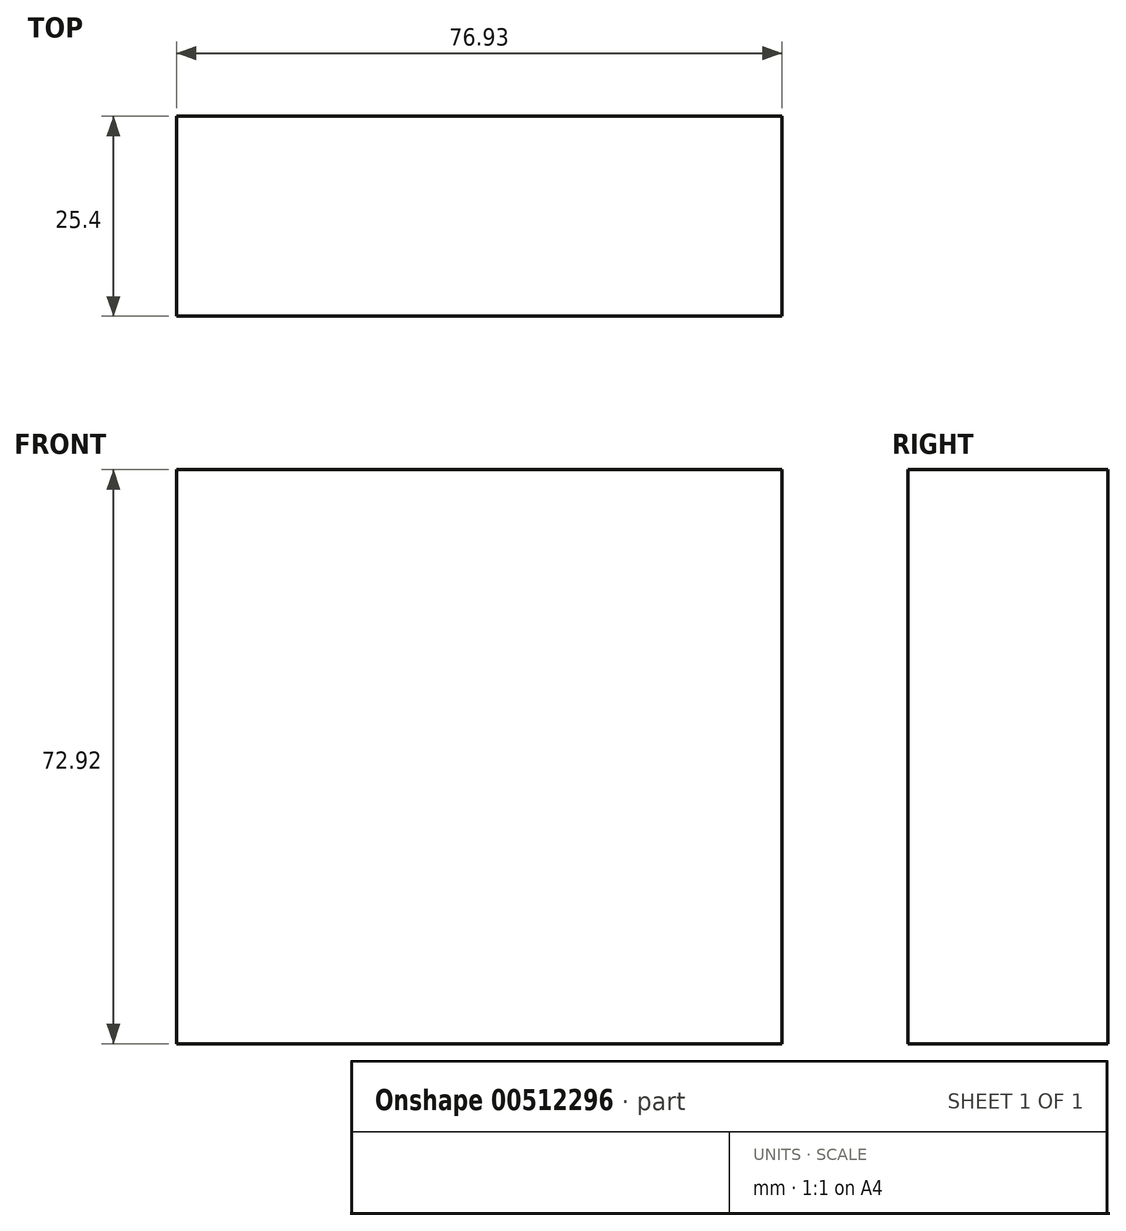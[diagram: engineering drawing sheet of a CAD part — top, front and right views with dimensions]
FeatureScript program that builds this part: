
annotation { "Feature Type Name" : "Feature", "Feature Type Description" : "" }
export const myFeature = defineFeature(function(context is Context, id is Id, definition is map)
    precondition{}
    {
        {
            var Q0;
            Q0=qCreatedBy(makeId("Front.planeOp"),FACE);
            var sketch = newSketch(context, id + "F0", { "sketchPlane" : qUnion([Q0])});
            skLineSegment(sketch, "E0.bottom", {"start": v(-34.07, 25.23) * mm, "end": v(42.86, 25.23) * mm});
            skLineSegment(sketch, "E0.top", {"start": v(-34.07, -47.7) * mm, "end": v(42.86, -47.7) * mm});
            skLineSegment(sketch, "E0.left", {"start": v(-34.07, 25.23) * mm, "end": v(-34.07, -47.7) * mm});
            skLineSegment(sketch, "E0.right", {"start": v(42.86, 25.23) * mm, "end": v(42.86, -47.7) * mm});
            skSolve(sketch);
        }
        {
            var Q0;
            Q0 = qSketchRegion(id + "F0", true);
            extrude(context, id + "F1", {"entities" : qUnion([Q0]), "depth" : 25.4 * mm});
        }
    });
